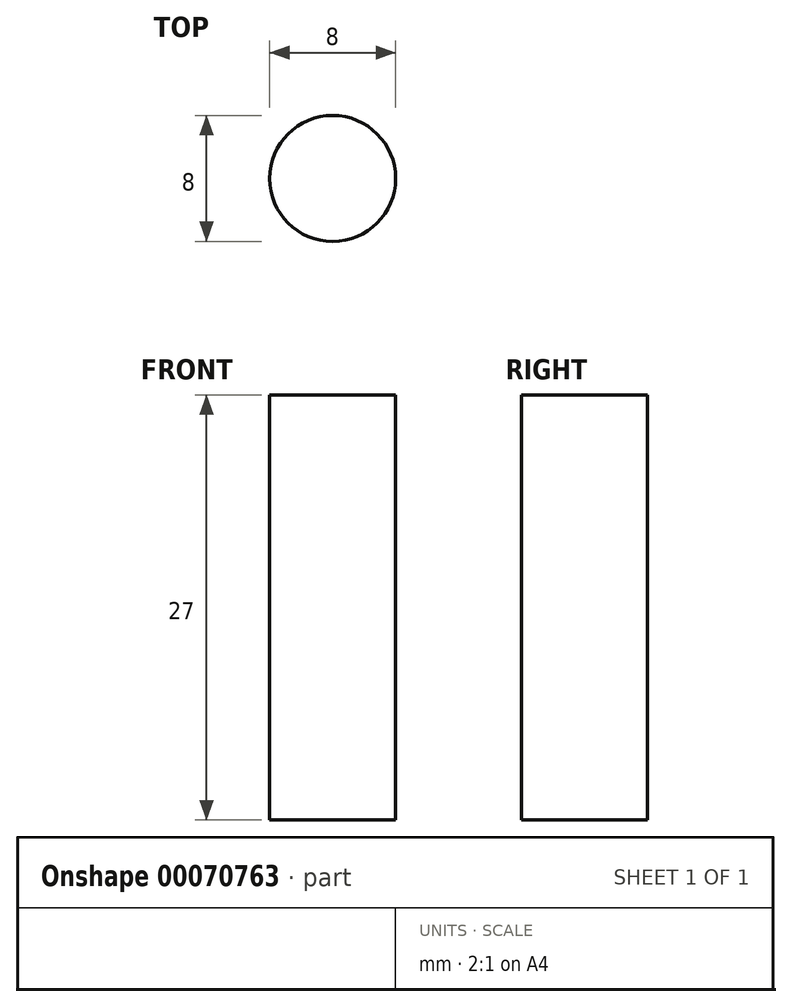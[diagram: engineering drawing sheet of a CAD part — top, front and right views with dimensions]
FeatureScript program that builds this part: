
annotation { "Feature Type Name" : "Feature", "Feature Type Description" : "" }
export const myFeature = defineFeature(function(context is Context, id is Id, definition is map)
    precondition{}
    {
        {
            var Q0;
            Q0=qCreatedBy(makeId("Top.planeOp"),FACE);
            var sketch = newSketch(context, id + "F0", { "sketchPlane" : qUnion([Q0])});
            skCircle(sketch, "E0", {"center": v(0, 0) * mm, "radius": 4 * mm});
            skSolve(sketch);
        }
        {
            var Q0;
            Q0=makeQuery(id+"F0.imprint","IMPRINT",FACE,{"disambiguationData":[TD([[makeQuery(id+"F0.imprint","IMPRINT",EDGE,{"derivedFrom":sQuery(id+"F0.wireOp",EDGE,"E0")}),1.0]])]});
            extrude(context, id + "F1", {"entities" : qUnion([Q0]), "depth" : 27 * mm});
        }
    });
